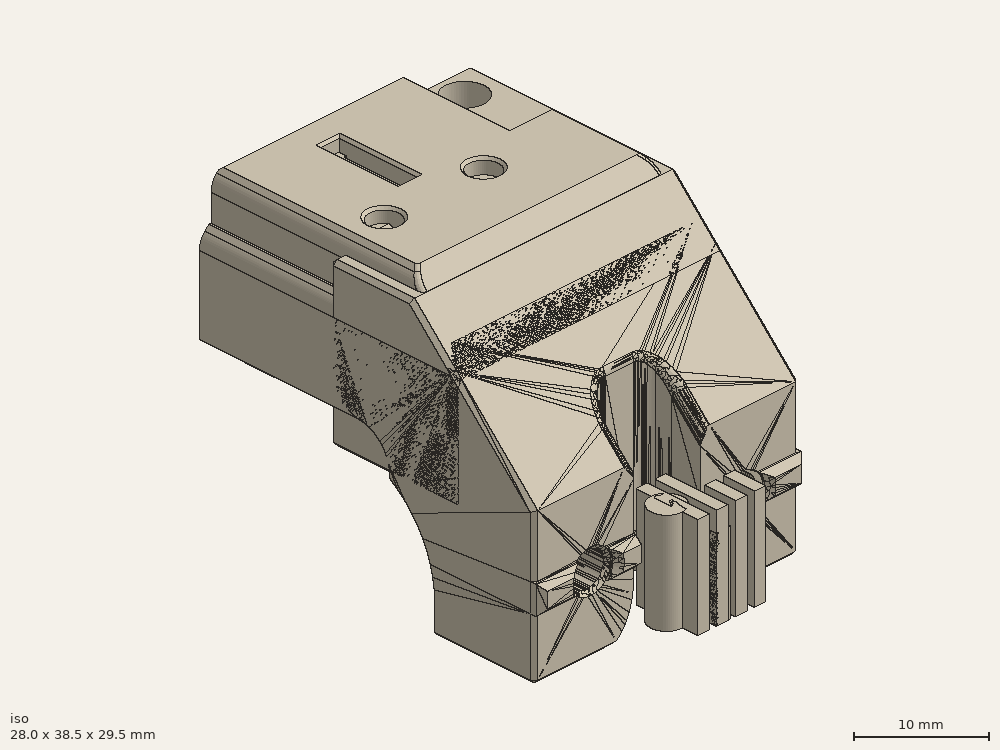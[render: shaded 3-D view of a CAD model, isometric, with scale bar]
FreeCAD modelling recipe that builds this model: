
FCSTD DOCUMENT  (FreeCAD 0.18R16146 (Git))
Label: z-belt-mount
License: All rights reserved
LicenseURL: http://en.wikipedia.org/wiki/All_rights_reserved
objects: Part::Box×17, Part::Cut×15, Part::Chamfer×11, Part::Feature×7, Part::Cylinder×7, Part::MultiFuse×6, App::Part×2
note: 63 computed .brp shape members not serialized (recipe doc carries the construction recipe); baked Part::Feature solids carry a one-line shape summary decoded from their .brp

FEATURE [Part::Feature] Part__Feature091  label="V0-BeltZ-BedMount-BETA4"
  Placement = pos=(-60,-119.95,45.15) rot=(0,0,1;0rad)
  shape: bbox 28.01 x 36.11 x 25.01 mm, 208 faces (baked)
FEATURE [Part::Box] Box  label="Cube"
  AttacherType = Attacher::AttachEngine3D
  Height = 16
  Length = 28
  Placement = pos=(-14,8,12) rot=(0,0,1;0rad)
  Width = 26.75
FEATURE [Part::Feature] Part__Feature093  label="V0-BeltZ-BeltClipTop-BETA4"
  Placement = pos=(-60.01,-119.9,45.15) rot=(0,0,1;0rad)
  shape: bbox 25.5 x 24.92 x 5.558 mm, 50 faces (baked)
FEATURE [Part::Box] Box002  label="Cube002"
  AttacherType = Attacher::AttachEngine3D
  Height = 16
  Length = 28
  Placement = pos=(-14,34.75,12) rot=(0,0,1;0rad)
  Width = 20
FEATURE [Part::Feature] Part__Feature094  label="V0-BeltZ-BedMount-BETA005"
  Placement = pos=(-60,-119.95,45.15) rot=(0,0,1;0rad)
  shape: bbox 28.01 x 36.11 x 25.01 mm, 208 faces (baked)
FEATURE [Part::Cut] Cut
  Base = -> Part__Feature094
  Tool = -> Box002
FEATURE [Part::Chamfer] Chamfer
  Base = -> Box
  Edges = 1 edges r=5: [Edge10]
FEATURE [Part::Box] Box003  label="Cube003"
  AttacherType = Attacher::AttachEngine3D
  Height = 23
  Length = 15
  Placement = pos=(-17.25,21.55,9) rot=(0,0,1;0rad)
  Width = 13.5
FEATURE [Part::Box] Box004  label="Cube004"
  AttacherType = Attacher::AttachEngine3D
  Height = 23
  Length = 15
  Placement = pos=(-17.25,21.55,9) rot=(0,0,1;0rad)
  Width = 13.5
FEATURE [Part::Cut] Cut003
  Base = -> Chamfer
  Tool = -> Box004
FEATURE [Part::Cut] Cut004
  Base = -> Cut
  Tool = -> Box003
FEATURE [Part::Chamfer] Chamfer001
  Base = -> Cut004
  Edges = 1 edges r=0.4: [Edge272]
FEATURE [Part::Chamfer] Chamfer002
  Base = -> Cut003
  Edges = 14 edges r=0.4: [Edge1,Edge2,Edge3,Edge4,Edge8,Edge9,Edge10,Edge11,Edge12,Edge14,Edge15,Edge17,Edge20,Edge21]
FEATURE [Part::Chamfer] Chamfer003
  Base = -> Chamfer001
  Edges = 1 edges r=0.4: [Edge75]
FEATURE [Part::Chamfer] Chamfer004
  Base = -> Chamfer003
  Edges = 1 edges r=0.4: [Edge41]
FEATURE [Part::Cylinder] Cylinder
  Angle = 360
  AttacherType = Attacher::AttachEngine3D
  Height = 25
  Placement = pos=(-7,28.15,20) rot=(0,1,0;1.5708rad)
  Radius = 1.65
FEATURE [Part::Cylinder] Cylinder001
  Angle = 360
  AttacherType = Attacher::AttachEngine3D
  Height = 2
  Placement = pos=(12,28.15,20) rot=(0,1,0;1.5708rad)
  Radius = 3.5
FEATURE [Part::Cut] Cut005
  Base = -> Chamfer002
  Tool = -> Cylinder
FEATURE [Part::Cylinder] Cylinder002
  Angle = 360
  AttacherType = Attacher::AttachEngine3D
  Height = 25
  Placement = pos=(-7,28.15,20) rot=(0,1,0;1.5708rad)
  Radius = 1.65
FEATURE [Part::Cut] Cut006
  Base = -> Chamfer004
  Tool = -> Cylinder002
FEATURE [Part::Box] Box005  label="Cube005"
  AttacherType = Attacher::AttachEngine3D
  Height = 8
  Length = 16
  Placement = pos=(-8,-6.5,0) rot=(0,0,1;0rad)
  Width = 13
FEATURE [Part::Box] Box006  label="Cube006"
  AttacherType = Attacher::AttachEngine3D
  Height = 8
  Length = 7
  Placement = pos=(-3.5,-3.25,0) rot=(0,0,1;0rad)
  Width = 6.5
FEATURE [Part::Cylinder] Cylinder004
  Angle = 360
  AttacherType = Attacher::AttachEngine3D
  Height = 10
  Radius = 1.65
FEATURE [Part::Box] Box008  label="Cube008"
  AttacherType = Attacher::AttachEngine3D
  Height = 8
  Length = 1.5
  Placement = pos=(2,-3.25,0) rot=(0,0,1;0rad)
  Width = 6.5
FEATURE [Part::Box] Box009  label="Cube009"
  AttacherType = Attacher::AttachEngine3D
  Height = 1.1
  Length = 12.2
  Placement = pos=(-6.1,4.5,5.9) rot=(0,0,1;0rad)
  Width = 2
FEATURE [Part::Box] Box010  label="Cube010"
  AttacherType = Attacher::AttachEngine3D
  Height = 12
  Length = 2
  Placement = pos=(-3.25,32.75,14) rot=(0,0,1;0rad)
  Width = 2
FEATURE [Part::Box] Box011  label="Cube011"
  AttacherType = Attacher::AttachEngine3D
  Height = 12
  Length = 2
  Placement = pos=(-3.25,21.55,14) rot=(0,0,1;0rad)
  Width = 2
FEATURE [Part::Chamfer] Chamfer005
  Base = -> Box011
  Edges = 2 edges r=1: [Edge2,Edge4]
FEATURE [Part::Chamfer] Chamfer006
  Base = -> Box010
  Edges = 2 edges r=1: [Edge2,Edge4]
FEATURE [Part::Box] Box012  label="Cube012"
  AttacherType = Attacher::AttachEngine3D
  Height = 1.1
  Length = 12.2
  Placement = pos=(-6.1,-6.5,5.9) rot=(0,0,1;0rad)
  Width = 2
FEATURE [Part::MultiFuse] Fusion002
  Shapes = -> [Box009,Box012]
FEATURE [Part::Chamfer] Chamfer007
  Base = -> Fusion002
  Edges = 4 edges r=1.09: [Edge4,Edge8,Edge16,Edge20]
  Placement = pos=(0,0,1) rot=(0,0,1;0rad)
FEATURE [Part::Box] Box013  label="Cube013"
  AttacherType = Attacher::AttachEngine3D
  Height = 0.3
  Length = 16
  Placement = pos=(-8,-3.25,7.7) rot=(0,0,1;0rad)
  Width = 6.5
FEATURE [Part::Box] Box014  label="Cube014"
  AttacherType = Attacher::AttachEngine3D
  Height = 3.5
  Length = 16
  Placement = pos=(-8,-3.25,0) rot=(0,0,1;0rad)
  Width = 6.5
FEATURE [Part::Box] Box015  label="Cube015"
  AttacherType = Attacher::AttachEngine3D
  Height = 10
  Length = 1.2
  Placement = pos=(0,-3.25,0) rot=(0,0,1;0rad)
  Width = 6.5
FEATURE [Part::Box] Box016  label="Cube016"
  AttacherType = Attacher::AttachEngine3D
  Height = 10
  Length = 1.2
  Placement = pos=(2,-3.25,0) rot=(0,0,1;0rad)
  Width = 6.5
FEATURE [Part::Box] Box017  label="Cube017"
  AttacherType = Attacher::AttachEngine3D
  Height = 10
  Length = 1.2
  Placement = pos=(4,-3.25,0) rot=(0,0,1;0rad)
  Width = 6.5
FEATURE [Part::Box] Box018  label="Cube018"
  AttacherType = Attacher::AttachEngine3D
  Height = 10
  Length = 1.2
  Placement = pos=(6,-3.25,0) rot=(0,0,1;0rad)
  Width = 6.5
FEATURE [Part::MultiFuse] Fusion003
  Shapes = -> [Box018,Box017,Box016,Box015]
FEATURE [Part::Feature] Fusion003001  label="Fusion004"
  Placement = pos=(4.3,0,0) rot=(0,0,1;0rad)
  shape: bbox 7.2 x 6.5 x 10 mm, 24 faces, 4 solids (baked)
FEATURE [Part::Feature] Fusion003002  label="Fusion005"
  Placement = pos=(-11.5,0,0) rot=(0,0,1;0rad)
  shape: bbox 7.2 x 6.5 x 10 mm, 24 faces, 4 solids (baked)
FEATURE [Part::MultiFuse] Fusion003003
  Placement = pos=(0,0,-5.7) rot=(0,0,1;0rad)
  Shapes = -> [Fusion003002,Fusion003001]
FEATURE [Part::Feature] Fusion003003001  label="Fusion003004"
  Placement = pos=(0,0,6.9) rot=(0,0,1;0rad)
  shape: bbox 23 x 6.5 x 10 mm, 48 faces, 8 solids (baked)
FEATURE [Part::Cylinder] Cylinder005
  Angle = 360
  AttacherType = Attacher::AttachEngine3D
  Height = 4
  Placement = pos=(10.5,31.8,24) rot=(0,0,1;0rad)
  Radius = 2
FEATURE [Part::Cylinder] Cylinder006
  Angle = 360
  AttacherType = Attacher::AttachEngine3D
  Height = 30
  Placement = pos=(10.5,31.8,8) rot=(0,0,1;0rad)
  Radius = 1.4
FEATURE [Part::Cylinder] Cylinder003
  Angle = 360
  AttacherType = Attacher::AttachEngine3D
  Height = 2
  Placement = pos=(12,28.15,20) rot=(0,1,0;1.5708rad)
  Radius = 3.5
FEATURE [Part::MultiFuse] Fusion001  label="mounter-pt3"
  Shapes = -> [Chamfer006,Chamfer005]
FEATURE [Part::Cut] Cut016
  Base = -> Cut005
  Tool = -> Cylinder001
FEATURE [Part::Cut] Cut017
  Base = -> Cut006
  Tool = -> Cylinder003
FEATURE [Part::MultiFuse] Fusion003003002
  Shapes = -> [Cylinder005,Cylinder006]
FEATURE [Part::Feature] Fusion003003002001  label="Fusion003003003"
  shape: bbox 4 x 4 x 30 mm, 7 faces (baked)
FEATURE [Part::Cut] Cut018
  Base = -> Cut016
  Tool = -> Fusion003003002
FEATURE [Part::Cut] Cut019  label="belt-mounter-pt-2"
  Base = -> Cut017
  Tool = -> Fusion003003002001
FEATURE [Part::MultiFuse] Fusion003003002002  label="belt-mounter-pt-1"
  Shapes = -> [Cut018,Fusion001]
FEATURE [Part::Cut] Cut020
  Base = -> Box005
  Tool = -> Box006
FEATURE [Part::Cut] Cut021
  Base = -> Cut020
  Tool = -> Chamfer007
FEATURE [Part::Cut] Cut022
  Base = -> Cut021
  Tool = -> Box013
FEATURE [Part::Cut] Cut023
  Base = -> Cut022
  Tool = -> Box014
FEATURE [Part::Cut] Cut024
  Base = -> Cut023
  Tool = -> Fusion003003001
FEATURE [Part::Cut] Cut025
  Base = -> Cut024
  Tool = -> Fusion003003
FEATURE [Part::Chamfer] Chamfer008
  Base = -> Cut025
  Edges = 2 edges: [Edge213 r1=0.2 r2=1,Edge239 r1=0.2 r2=1]
FEATURE [Part::Chamfer] Chamfer009
  Base = -> Chamfer008
  Edges = 2 edges: [Edge55 r1=1 r2=0.2,Edge57 r1=1 r2=0.2]
FEATURE [Part::Chamfer] Chamfer010  label="belt-holder"
  Base = -> Chamfer009
  Edges = 8 edges r=0.4: [Edge56,Edge64,Edge118,Edge119,Edge123,Edge137,Edge138,Edge141]
  Placement = pos=(-10.3,28.2,20.1) rot=(0,1,0;1.5708rad)
FEATURE [App::Part] Part  label="belt-mounter-main-body"
  Group = -> [Chamfer006,Cut005,Chamfer005,Box010,Box011,Cylinder,Box004,Chamfer,Cylinder001,Cut016,Chamfer002,Cut003,Fusion001,Fusion003003002,Box,Cylinder005,Cylinder006,Cut018,Fusion003003002002,Chamfer004,Chamfer003,Part__Feature094,Cut006,Cut,Cut017,Box003,Box002,Cylinder002,Chamfer001,Cut004,Cylinder003,Fusion003003002001,Cut019]
  Origin = -> Origin
FEATURE [App::Part] Part001  label="belt-mounter-clamp"
  Group = -> [Box012,Chamfer007,Box005,Box009,Fusion002,Box006,Fusion003003,Box013,Box014,Fusion003001,Fusion003002,Fusion003003001,Cut020,Cut021,Cut022,Cut023,Cut024,Cut025,Chamfer008,Chamfer009,Chamfer010]
  Origin = -> Origin001
